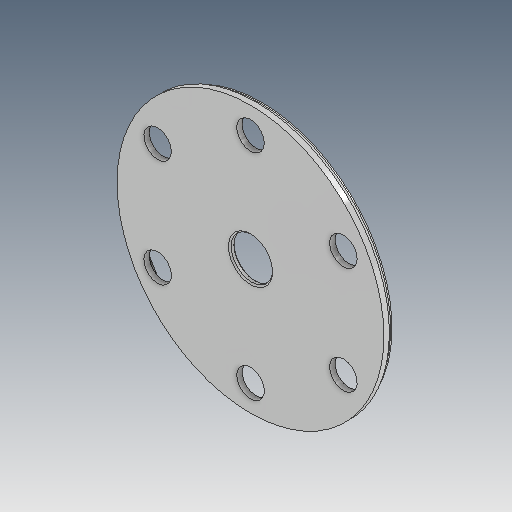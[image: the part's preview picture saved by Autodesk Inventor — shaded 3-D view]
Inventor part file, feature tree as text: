
AUTODESK INVENTOR PART (.ipt)
format: ipt  version: 2020.3 (Build 243373010, 373A)  size: 166,912 bytes
history: native  units: mm
features: sketch x2, revolve x1, hole x1, pattern_circular x1, chamfer x1, projected_geometry x1
ambient origin geometry x8: Origin, YZ Plane, XZ Plane, XY Plane, X Axis, Y Axis, Z Axis, Center Point
bodies: Body1 (feature_tree)
feature tree (7):
  revolve  "Revolution1"  [1 undecoded]
  hole  "Hole1"  [1 undecoded]
  pattern_circular  "Circular Pattern1"  [2 undecoded]
  chamfer  "Chamfer1"  Distance=48.5mm
  sketch  "Sketch2"  dims[d3=1.0mm d4=25.307274mm]
  sketch  "Sketch3"  dims[d5=0.75mm d7=0.25mm d8=2.0mm d10=48.5mm d11=47.449689mm d12=1.25mm d13=7.525mm d14=90.0deg d15=19.5mm d16=48.5mm d17=5.0mm d18=30.0mm d19=4.0mm d20=2.0mm d21=90.0deg d22=8.0mm d23=120.0deg d24=60.0mm d25=360.0deg d27=0.25mm d28=2.0mm d29=45.0deg]
  projected_geometry  "Projected Loop1"
note: 4 required parameter values undecoded (feature->parameter linkage not recoverable at this tier; creation-order binding heuristic only, values carry confidence <= 0.55)